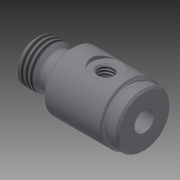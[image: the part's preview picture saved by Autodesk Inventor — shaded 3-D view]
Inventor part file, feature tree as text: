
AUTODESK INVENTOR PART (.ipt)
format: ipt  version: 2014 (Build 180170000, 170)  size: 246,784 bytes
history: native  units: in
note: dims shown in document units (in); Inventor stores cm internally (conversion verified against a paired STEP export)
features: other x84, sketch x5, revolve x4, thread x2, hole x1
ambient origin geometry x8: Origin, YZ Plane, XZ Plane, XY Plane, X Axis, Y Axis, Z Axis, Center Point
bodies: Solid1 (feature_tree)
feature tree (96):
  revolve  "Revolution1"  [1 undecoded]
  thread  "Thread1"  [1 undecoded]
  revolve  "Revolution2"  Angle=360.0deg
  hole  "Hole1"  [1 undecoded]
  revolve  "Revolution3"  [1 undecoded]
  thread  "Thread2"  [1 undecoded]
  revolve  "Revolution4"  [1 undecoded]
  other  "c2_XY"
  other  "c2_YZ"
  other  "c2_ZX"
  other  "c2_X"
  other  "c2_Y"
  other  "c2_Z"
  other  "c2_Center"
  other  "e2_XY"
  other  "e2_YZ"
  other  "e2_ZX"
  other  "e2_X"
  other  "e2_Y"
  other  "e2_Z"
  other  "e2_Center"
  other  "f1_XY"
  other  "f1_YZ"
  other  "f1_ZX"
  other  "f1_X"
  other  "f1_Y"
  other  "f1_Z"
  other  "f1_Center"
  other  "f2_XY"
  other  "f2_YZ"
  other  "f2_ZX"
  other  "f2_X"
  other  "f2_Y"
  other  "f2_Z"
  other  "f2_Center"
  other  "i1_XY"
  other  "i1_YZ"
  other  "i1_ZX"
  other  "i1_X"
  other  "i1_Y"
  other  "i1_Z"
  other  "i1_Center"
  other  "i2_XY"
  other  "i2_YZ"
  other  "i2_ZX"
  other  "i2_X"
  other  "i2_Y"
  other  "i2_Z"
  other  "i2_Center"
  other  "l1_XY"
  other  "l1_YZ"
  other  "l1_ZX"
  other  "l1_X"
  other  "l1_Y"
  other  "l1_Z"
  other  "l1_Center"
  other  "l2_XY"
  other  "l2_YZ"
  other  "l2_ZX"
  other  "l2_X"
  other  "l2_Y"
  other  "l2_Z"
  other  "l2_Center"
  other  "rod_guide_XY"
  other  "rod_guide_YZ"
  other  "rod_guide_ZX"
  other  "rod_guide_X"
  other  "rod_guide_Y"
  other  "rod_guide_Z"
  other  "rod_guide_Center"
  other  "to_mounting_bracket_XY"
  other  "to_mounting_bracket_YZ"
  other  "to_mounting_bracket_ZX"
  other  "to_mounting_bracket_X"
  other  "to_mounting_bracket_Y"
  other  "to_mounting_bracket_Z"
  other  "to_mounting_bracket_Center"
  other  "to_rod_XY"
  other  "to_rod_YZ"
  other  "to_rod_ZX"
  other  "to_rod_X"
  other  "to_rod_Y"
  other  "to_rod_Z"
  other  "to_rod_Center"
  other  "to_tube_XY"
  other  "to_tube_YZ"
  other  "to_tube_ZX"
  other  "to_tube_X"
  other  "to_tube_Y"
  other  "to_tube_Z"
  other  "to_tube_Center"
  sketch  "Sketch_2"  dims[d0=360.0deg d1=0.1557in d2=0.0in d3=360.0deg]
  sketch  "Sketch_3"  dims[d4=0.21in d5=0.75in d6=0.25in d7=0.25in d8=90.0deg d9=1.156in d10=0.0in d11=360.0deg]
  sketch  "Sketch3"  dims[d12=0.0955in d13=0.1018in d14=360.0deg]
  sketch  "Sketch_13"
  sketch  "Sketch_47"
note: 6 required parameter values undecoded (feature->parameter linkage not recoverable at this tier; creation-order binding heuristic only, values carry confidence <= 0.55)